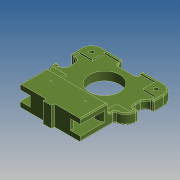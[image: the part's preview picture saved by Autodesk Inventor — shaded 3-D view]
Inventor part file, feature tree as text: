
AUTODESK INVENTOR PART (.ipt)
format: ipt  version: 2019 (Build 230136000, 136)  size: 669,696 bytes
history: native  units: mm
features: fillet x15, sketch x14, extrude x9, projected_geometry x6, hole x5, mirror x4, other x1
ambient origin geometry x8: Origin, YZ Plane, XZ Plane, XY Plane, X Axis, Y Axis, Z Axis, Center Point
bodies: Solid2 (feature_tree)
feature tree (54):
  extrude  "Extrusion2"  Depth=3.0mm
  extrude  "Extrusion3"  Depth=10.0mm TaperAngle=0.0deg
  hole  "Trou pour ressort"  [1 undecoded]
  mirror  "Mirror1"
  extrude  "Extrusion5"  Depth=3.0mm
  extrude  "Extrusion6"  Depth=2.0mm TaperAngle=0.0deg
  fillet  "Fillet3"  Radius=3.0mm
  hole  "Hole5"  [1 undecoded]
  extrude  "Extrusion13"  Depth=10.0mm TaperAngle=0.0deg
  other  "Work Axis2"
  hole  "Hole12"  [1 undecoded]
  mirror  "Mirror4"
  hole  "Hole16"  [1 undecoded]
  extrude  "Extrusion20"  Depth=41.0mm
  fillet  "Fillet30"  Radius=41.0mm
  fillet  "Fillet31"  Radius=20.0mm
  extrude  "Extrusion21"  Depth=10.0mm TaperAngle=0.0deg
  extrude  "Extrusion22"  Depth=10.0mm
  fillet  "Fillet32"  Radius=10.0mm
  fillet  "Fillet33"  Radius=76.2mm
  mirror  "Mirror6"
  fillet  "Fillet34"  Radius=26.0mm
  fillet  "Fillet35"  Radius=1.5mm
  extrude  "Extrusion23"  Depth=50.5mm
  fillet  "Fillet36"  Radius=50.5mm
  fillet  "Fillet37"  Radius=8.0mm
  fillet  "Fillet38"  Radius=15.0mm
  fillet  "Fillet39"  Radius=2.0mm
  fillet  "Fillet42"  Radius=1.0mm
  hole  "Hole17"  [1 undecoded]
  mirror  "Mirror7"
  fillet  "Fillet43"  Radius=5.0mm
  fillet  "Fillet45"  Radius=1.0mm
  fillet  "Fillet46"  Radius=20.0mm
  sketch  "Sketch1"  dims[d14=20.0mm d15=20.0mm d16=0.0mm d19=3.0mm]
  sketch  "Sketch3"  dims[d20=5.0mm d21=10.0mm d22=0.0mm]
  sketch  "Sketch6"  dims[d42=22.0mm d43=4.1mm]
  sketch  "Sketch8"  dims[d44=30.0mm d45=3.0mm]
  sketch  "Sketch9"  dims[d49=4.0mm]
  sketch  "Sketch12"  dims[d50=5.0mm d51=6.0mm d52=4.0mm d53=2.0mm d54=90.0deg d55=8.0mm d56=20.594885mm d60=2.0mm d61=0.0mm d62=3.0mm]
  sketch  "Sketch22"  dims[d66=16.0mm d67=58.0mm d68=0.0mm]
  sketch  "Sketch29"  dims[d78=11.5mm]
  projected_geometry  "Projected Loop2"
  sketch  "Sketch36"  dims[d79=6.0mm d80=6.0mm d81=4.0mm d82=2.0mm d83=90.0deg d84=8.0mm d85=20.594885mm d147=10.0mm d148=0.0mm]
  sketch  "Sketch38"  dims[d205=3.0mm]
  sketch  "Sketch39"  dims[d206=1.5mm d207=6.0mm d208=4.0mm d209=2.0mm d210=90.0deg d211=2.0mm d212=20.594885mm d213=10.0mm]
  sketch  "Sketch40"  dims[d245=20.0mm d246=17.0mm]
  sketch  "Sketch41"  dims[d258=32.0mm]
  sketch  "Sketch43"  dims[d259=30.0mm d260=6.0mm d261=4.0mm d262=2.0mm d263=90.0deg d264=8.0mm d265=20.594885mm d266=41.0mm d267=41.0mm d272=20.0mm d273=10.0mm d274=0.0mm d275=10.0mm d276=10.0mm d277=76.2mm d278=26.0mm d279=1.5mm d280=0.0mm d281=50.5mm d282=50.5mm d283=8.0mm d284=15.0mm d285=2.0mm d286=0.0mm d287=1.0mm d288=5.0mm d289=5.0mm d290=1.0mm d291=20.0mm d292=6.0mm d293=2.0mm d294=0.0mm d295=1.0mm d296=2.0mm d297=2.0mm d298=1.0mm d303=1.0mm d304=32.0mm d305=51.0mm d306=4.0mm d307=6.0mm d308=4.0mm d309=2.0mm d310=90.0deg d311=8.0mm d312=20.594885mm d313=2.0mm d315=2.0mm d316=1.0mm]
  projected_geometry  "Project Cut Edges2"
  projected_geometry  "Project Cut Edges4"
  projected_geometry  "Project Cut Edges5"
  projected_geometry  "Project Cut Edges7"
  projected_geometry  "Project Cut Edges9"
note: 5 required parameter values undecoded (feature->parameter linkage not recoverable at this tier; creation-order binding heuristic only, values carry confidence <= 0.55)
